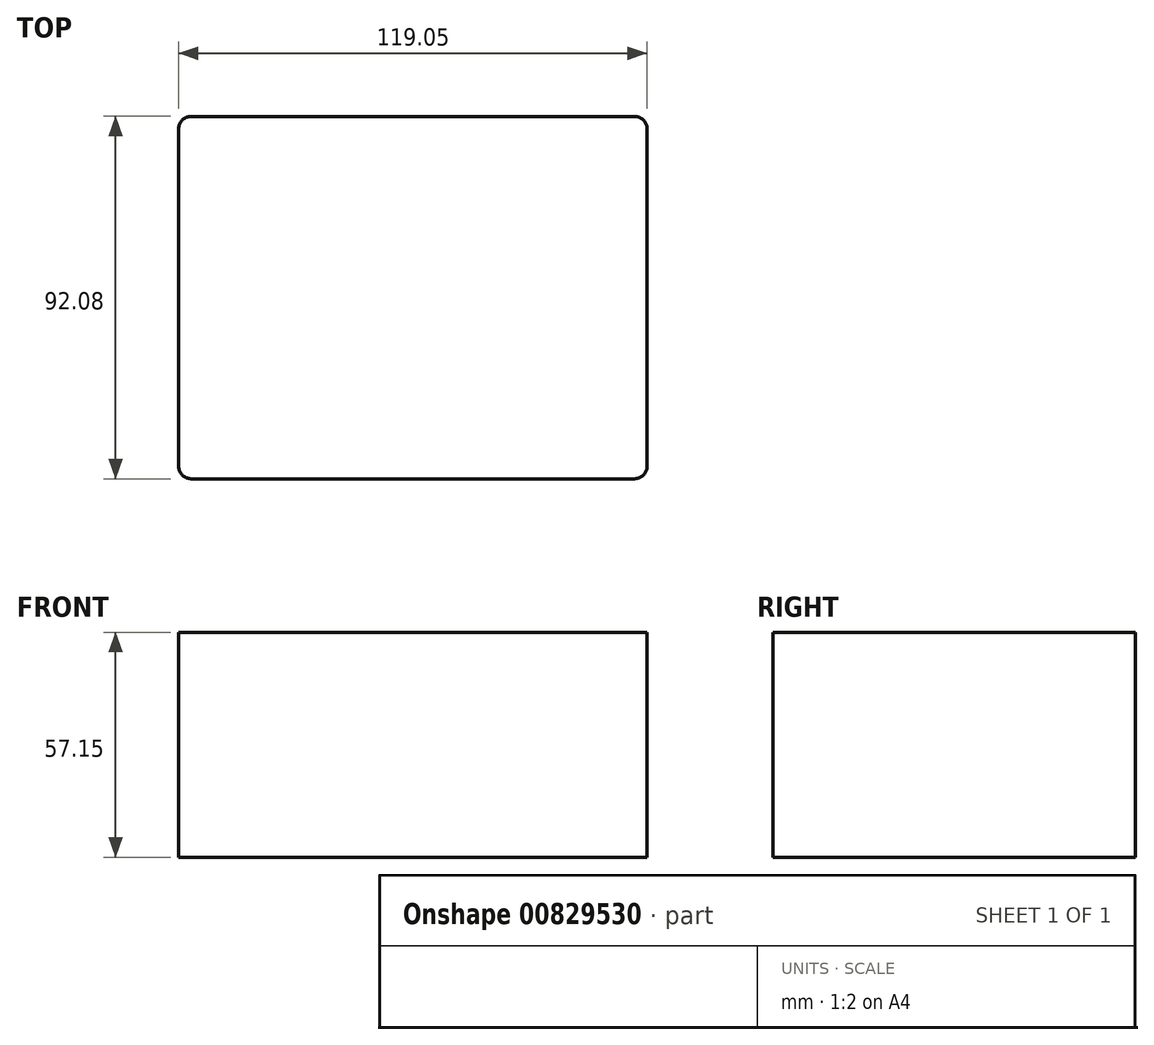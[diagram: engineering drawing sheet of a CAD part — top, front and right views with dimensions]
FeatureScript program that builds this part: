
annotation { "Feature Type Name" : "Feature", "Feature Type Description" : "" }
export const myFeature = defineFeature(function(context is Context, id is Id, definition is map)
    precondition{}
    {
        {
            var Q0;
            Q0=qCreatedBy(makeId("Top.planeOp"),FACE);
            var sketch = newSketch(context, id + "F0", { "sketchPlane" : qUnion([Q0])});
            skLineSegment(sketch, "E0.bottom", {"start": v(3.17, 0) * mm, "end": v(115.87, 0) * mm});
            skLineSegment(sketch, "E0.top", {"start": v(3.17, 92.08) * mm, "end": v(115.87, 92.08) * mm});
            skLineSegment(sketch, "E0.left", {"start": v(0, 3.17) * mm, "end": v(0, 88.9) * mm});
            skLineSegment(sketch, "E0.right", {"start": v(119.05, 3.17) * mm, "end": v(119.05, 88.9) * mm});
            skPoint(sketch, "E1.visualSharp", {"position": v(0, 92.08) * mm});
            skArc(sketch, "E1.filletArc", {"start": v(3.17, 92.08) * mm, "mid": v(0.93, 91.15) * mm, "end": v(0, 88.9) * mm});
            skPoint(sketch, "E2.visualSharp", {"position": v(119.05, 92.08) * mm});
            skArc(sketch, "E2.filletArc", {"start": v(119.05, 88.9) * mm, "mid": v(118.12, 91.15) * mm, "end": v(115.87, 92.08) * mm});
            skPoint(sketch, "E3.visualSharp", {"position": v(119.05, 0) * mm});
            skArc(sketch, "E3.filletArc", {"start": v(115.87, 0) * mm, "mid": v(118.12, 0.93) * mm, "end": v(119.05, 3.17) * mm});
            skPoint(sketch, "E4.visualSharp", {"position": v(0, 0) * mm});
            skArc(sketch, "E4.filletArc", {"start": v(0, 3.17) * mm, "mid": v(0.93, 0.93) * mm, "end": v(3.17, 0) * mm});
            skSolve(sketch);
        }
        {
            var Q0;
            Q0=makeQuery(id+"F0.imprint","IMPRINT",FACE,{"disambiguationData":[TD([[makeQuery(id+"F0.imprint","IMPRINT",EDGE,{"derivedFrom":sQuery(id+"F0.wireOp",EDGE,"E0.bottom")}),1.0]])]});
            extrude(context, id + "F1", {"entities" : qUnion([Q0]), "depth" : 57.15 * mm, "offsetDistance" : 25.4 * mm});
        }
    });
